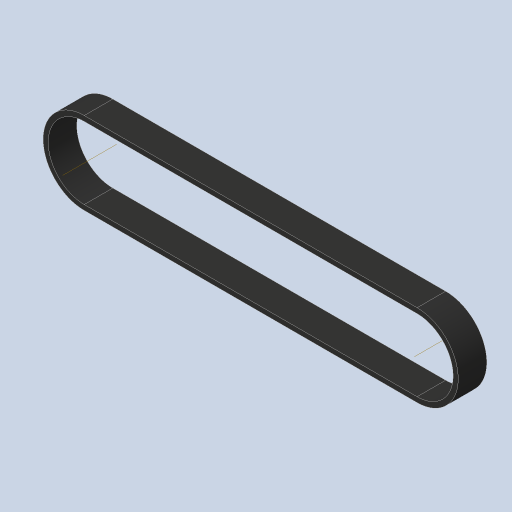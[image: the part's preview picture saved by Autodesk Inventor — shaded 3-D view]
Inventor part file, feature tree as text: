
AUTODESK INVENTOR PART (.ipt)
format: ipt  version: 2023.4 (Build 274418000, 418)  size: 163,328 bytes
history: native  units: in
note: dims shown in document units (in); Inventor stores cm internally (conversion verified against a paired STEP export)
features: sketch x3, extrude x1, other x1, projected_geometry x1
ambient origin geometry x8: Origin, YZ Plane, XZ Plane, XY Plane, X Axis, Y Axis, Z Axis, Center Point
bodies: Body1 (feature_tree)
feature tree (6):
  sketch  "Sketch2"  dims[d0=0.9023in d1=0.9023in]
  extrude  "Extrusion2"  Depth=0.9023in
  sketch  "Sketch5"  dims[d3=1.4174in d5=3.8976in d9=0.0787in d10=0.0598in d11=0.0299in d12=0.0219in d13=0.0219in d14=0.0059in d15=0.0059in d20=0.3346in d21=0.0in d22=0.0787in d23=0.0598in d24=0.0299in d25=0.0219in d26=0.0219in d27=0.0059in d28=0.0059in d29=0.0299in d30=0.0394in d31=0.0787in d32=0.0232in d34=0.0219in d35=0.0in d36=0.0in d37=0.0059in d38=0.0022in d39=0.0022in d40=0.0in d41=0.0in d42=0.0081in d43=0.0081in d44=0.0299in]
  other  "Work Axis1"
  sketch  "Sketch4"  dims[d2=1.4174in]
  projected_geometry  "Projected Loop1"
